# Revit family: New Vetro 90
name_source: partatom
category: Equipamento especial
revit_build: Autodesk Revit 2016 (Build: 20150220_1215(x64)
units: mm (PartAtom-declared; Revit-internal decimal feet)

## family parameters
Compartilhado = Não
Corte com vazios quando carregados = Não
Cota do conector redondo = Utilizar diâmetro
Hospedeiro = Parede
Número OmniClass = 23.40.40.14.17.11
Ponto de cálculo do ambiente = Não
Sempre na vertical = Sim
Tipo de parte = Normal
Título OmniClass = Cookers, Ovens, Stoves

## types (2) — shared parameters
Atendimento ao Cliente = http://www.tramontina.com.br
Classe da Construção = CLASSE I
Código da Peça = 95800
Descrição = New Vetro 90
Desenvolvedor da Biblioteca = Factory Cursos e Desenvolvimento
Disjuntor Termomagnético = 10 A
Fabricante = Tramontina
Filtro de Aluminio (Lavavel) = 1
Filtro de Carvao Ativado = 2
Frequência = 60 Hz
Grau de Proteção = IPXO
Iluminação = 2 x 1,5 W - 12 V - Lâmpadas LED
Linha = Vetro Black Touch
Modelo = 95800
Numero de Velocidades = 3
Nível de Ruído = 64 dB (A) - cfe. Norma EN 60704
Peso Bruto (Kg) = 20.6
Peso Líquido (Kg) = 17.4
Potência Elétrica = 225 W
Potência do Motor = 220 W
Produto = New Vetro 90
Segmento = Residencial
Site do Desenvolvedor = www.factorycursos.com.br
URL = http://http:
Vazão Máxima = 620 m³/h - cfe. Norma IEC 61591

## per-type parameters (varying)
| type | Tensão |
| New Vetro 90 - 220 V | 220 V |
| New Vetro - 110 V | 127 V |

## geometry (parser evidence)
native form markers: Sweep x2
no freeform markers — native parametric forms only
